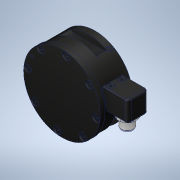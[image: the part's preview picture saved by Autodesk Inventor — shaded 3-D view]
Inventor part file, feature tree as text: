
AUTODESK INVENTOR PART (.ipt)
format: ipt  version: 2020.5 (Build 245400000, 400)  size: 993,792 bytes
history: imported  units: in
note: dims shown in document units (in); Inventor stores cm internally (conversion verified against a paired STEP export)
features: imported_body x6, sketch x1
ambient origin geometry x8: Origin, YZ Plane, XZ Plane, XY Plane, X Axis, Y Axis, Z Axis, Center Point
bodies: Solid1 (imported_parasolid), Solid2 (imported_parasolid), Solid3 (imported_parasolid), Solid4 (imported_parasolid), Solid5 (imported_parasolid)
feature tree (7):
  sketch  "Sketch1"
  imported_body  "Imported1"
  imported_body  "Imported2"
  imported_body  "Imported3"
  imported_body  "Imported4"
  imported_body  "Imported5"
  imported_body  NMx_Import_Brep_tag  [imported B-rep: ~80 faces, bbox_mm=[93.471978, 48.990206, 25.6924]]
